# Revit family: LG_MultiV_R32_IDU_Wall_Mounted(Standard)_SJ_NA_v1.3_NA
name_source: partatom
category: Mechanical Equipment
units: mm (PartAtom-declared; Revit-internal decimal feet)

## family parameters
Always vertical = Yes
Classification = None
Cut with Voids When Loaded = No
Part Type = Normal
Room Calculation Point = No
Round Connector Dimension = Use Diameter
Shared = No
Work Plane-Based = No

## types (5) — shared parameters
Air Flow Rate (H/M/L)(CMM) = -
Chassis name = SJ
Condensate Drain Connection Diameter = 5/8"
Default Elevation = 0"
Dimensions (WxHxD)(mm) = 837 x 308 x 189
Fan Motor Output (W) = 30
Fan Motor Type = BLDC
Fan Type = Cross Flow Fan
MCA (A) = 0.31
Net Weight (kg) = 8.9
Net Weight (lbs) = 19.6
Pipe Connection_Drain Side (inch) = 5/8
Pipe Connection_Drain Side (mm) = 16
Pipe Connection_Liquid Side (inch) = 1/4
Pipe Connection_Liquid Side (mm) = 6.35
Power Input (Heating)(W) = -
Power Supply (Ph_V_Hz) = 1, 208/230, 60
Refrigerant Liquid Connection Diameter = 1/4"
Refrigerant Type = R32
Running Current (A) = 0.25
Type = Wall Mount (Standard)

## per-type parameters (varying)
| type | Air Flow Rate (H/M/L)(CFM) | Cooling Capacity (Btu/h) | Cooling Capacity (kW) | Dimensions (WxHxD)(inch) | Heating Capacity (Btu/h) | Heating Capacity (kW) | MFA (A) | Pipe Connection_Gas Side (inch) | Pipe Connection_Gas Side (mm) | Power Input (Cooling)(W) | Refrigerant Gas Connection Diameter | Sound Pressure Level (H/M/L)(dB(A)) |
| ZRNU053SJSA | 240 / 230 / 208 | 5500 | 1.60 | 32-15/16 x 12-1/8 x 7-7/16 | 6100 | 1.80 | 15.0 | 3/8 | 9.52 | 11 / 10 / 9 | 3/8" | 30 / 29 / 28 |
| ZRNU073SJSA | 254 / 240 / 208 | 7500 | 2.20 | 32-15/16 x 12-1/8 x 7-7/16 | 8500 | 2.50 | 15.0 | 3/8 | 9.52 | 12 / 11 / 9 | 3/8" | 32 / 30 / 28 |
| ZRNU093SJSA | 275 / 254 / 208 | 9600 | 2.80 | 32-15/16 x 12-1/8 x 7/7-16 | 10900 | 3.20 | 15.0 | 3/8 | 9.52 | 13 / 12 / 9 | 3/8" | 34 / 32 / 28 |
| ZRNU123SJSA | 300 / 254 / 240 | 12300 | 3.60 | 32-15/16 x 12-1/8 x 7-7/16 | 13600 | 4.00 | 15.0 | 3/8 | 9.52 | 15 / 13 / 11 | 3/8" | 37 / 34 / 30 |
| ZRNU153SJSA | 371 / 336 / 240 | 15400 | 4.50 | 32-15/16 x 12-1/8 x 7-7/16 | 17100 | 5.00 | 15 | 1/2 | 12.7 | 23 / 18 / 11 | 1/2" | 42 / 39 / 32 |

note: column(s) folded — value = type name in every type: Model name

## geometry (parser evidence)
native form markers: Sweep x3
no freeform markers — native parametric forms only
